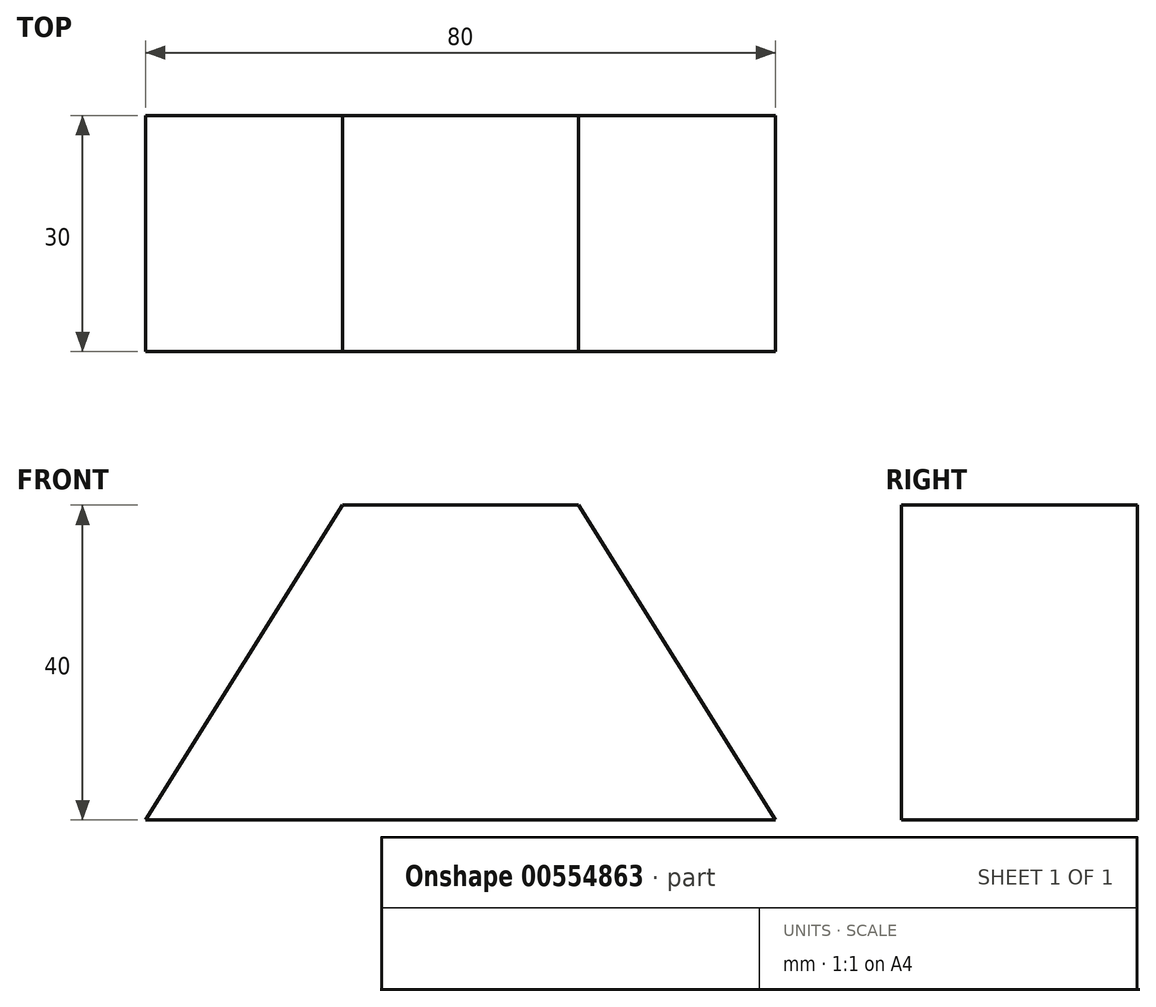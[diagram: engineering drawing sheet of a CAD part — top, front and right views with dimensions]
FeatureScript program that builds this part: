
annotation { "Feature Type Name" : "Feature", "Feature Type Description" : "" }
export const myFeature = defineFeature(function(context is Context, id is Id, definition is map)
    precondition{}
    {
        {
            var Q0;
            Q0=qCreatedBy(makeId("Front.planeOp"),FACE);
            var sketch = newSketch(context, id + "F0", { "sketchPlane" : qUnion([Q0])});
            skLineSegment(sketch, "E0", {"start": v(-32.43, 57.9) * mm, "end": v(-2.43, 57.9) * mm});
            skLineSegment(sketch, "E1", {"start": v(-2.43, 57.9) * mm, "end": v(22.57, 17.9) * mm});
            skLineSegment(sketch, "E2", {"start": v(22.57, 17.9) * mm, "end": v(-57.43, 17.9) * mm});
            skLineSegment(sketch, "E3", {"start": v(-57.43, 17.9) * mm, "end": v(-32.43, 57.9) * mm});
            skSolve(sketch);
        }
        {
            var Q0;
            Q0 = qSketchRegion(id + "F0", true);
            var Q1;
            Q1=makeQuery(id+"F0.imprint","IMPRINT",FACE,{"disambiguationData":[TD([[makeQuery(id+"F0.imprint","IMPRINT",EDGE,{"derivedFrom":sQuery(id+"F0.wireOp",EDGE,"E0")}),-1.0]])]});
            extrude(context, id + "F1", {"entities" : qUnion([Q0, Q1]), "depth" : 30 * mm, "offsetDistance" : 25 * mm});
        }
    });
